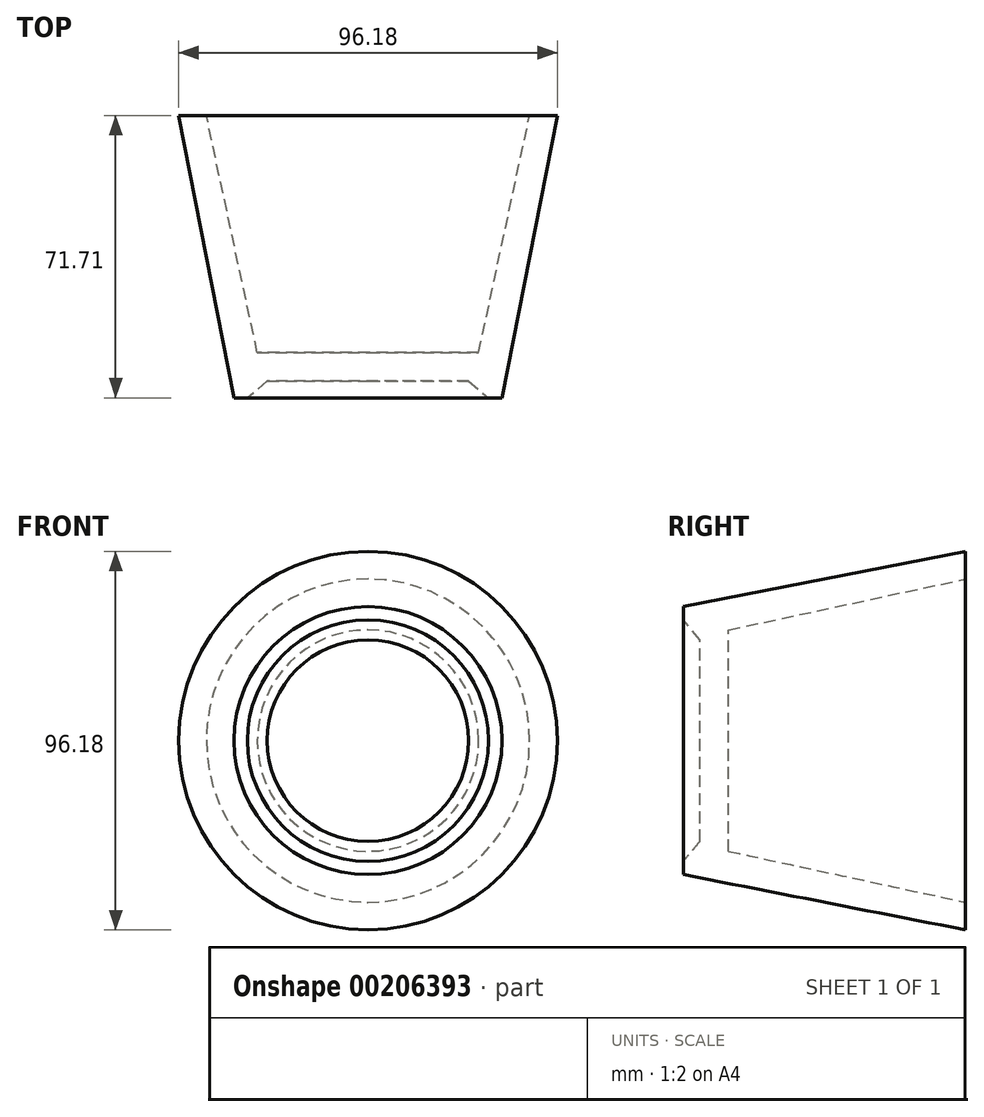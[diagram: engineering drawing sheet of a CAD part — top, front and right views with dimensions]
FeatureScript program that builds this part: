
annotation { "Feature Type Name" : "Feature", "Feature Type Description" : "" }
export const myFeature = defineFeature(function(context is Context, id is Id, definition is map)
    precondition{}
    {
        {
            var Q0;
            Q0=qCreatedBy(makeId("Top.planeOp"),FACE);
            var sketch = newSketch(context, id + "F0", { "sketchPlane" : qUnion([Q0])});
            skLineSegment(sketch, "E0", {"start": v(0, -36.98) * mm, "end": v(25.6, -36.98) * mm});
            skLineSegment(sketch, "E1", {"start": v(25.6, -36.98) * mm, "end": v(30.65, -41.2) * mm});
            skLineSegment(sketch, "E2", {"start": v(30.65, -41.2) * mm, "end": v(34.03, -41.2) * mm});
            skLineSegment(sketch, "E3", {"start": v(34.03, -41.2) * mm, "end": v(48.1, 30.51) * mm});
            skLineSegment(sketch, "E4", {"start": v(48.1, 30.51) * mm, "end": v(41.06, 30.51) * mm});
            skLineSegment(sketch, "E5", {"start": v(41.06, 30.51) * mm, "end": v(28.12, -29.67) * mm});
            skLineSegment(sketch, "E6", {"start": v(28.12, -29.67) * mm, "end": v(0, -29.67) * mm});
            skLineSegment(sketch, "E7", {"start": v(0, -36.98) * mm, "end": v(0, -29.67) * mm});
            skSolve(sketch);
        }
        {
            var Q0;
            Q0=makeQuery(id+"F0.imprint","IMPRINT",FACE,{"disambiguationData":[TD([[makeQuery(id+"F0.imprint","IMPRINT",EDGE,{"derivedFrom":sQuery(id+"F0.wireOp",EDGE,"E0")}),1.0]])]});
            var Q1;
            Q1=sQuery(id+"F0.wireOp",EDGE,"E7");
            revolve(context, id + "F1", {"entities" : qUnion([Q0]), "axis" : qUnion([Q1]), "revolveType" : RevolveType.FULL});
        }
    });
